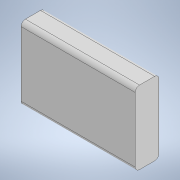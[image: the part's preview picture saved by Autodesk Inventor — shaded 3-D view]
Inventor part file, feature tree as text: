
AUTODESK INVENTOR PART (.ipt)
format: ipt  version: 2021 (Build 250183000, 183)  size: 97,280 bytes
history: native  units: mm
features: extrude x1, fillet x1, sketch x1
ambient origin geometry x8: Origin, YZ Plane, XZ Plane, XY Plane, X Axis, Y Axis, Z Axis, Center Point
bodies: Solid1 (feature_tree)
feature tree (3):
  extrude  "Extrusion1"  Depth=34.0mm
  fillet  "Fillet1"  Radius=11.0mm
  sketch  "Sketch1"  dims[d0=53.0mm d1=34.0mm d2=11.0mm d3=0.0mm d4=2.0mm]
